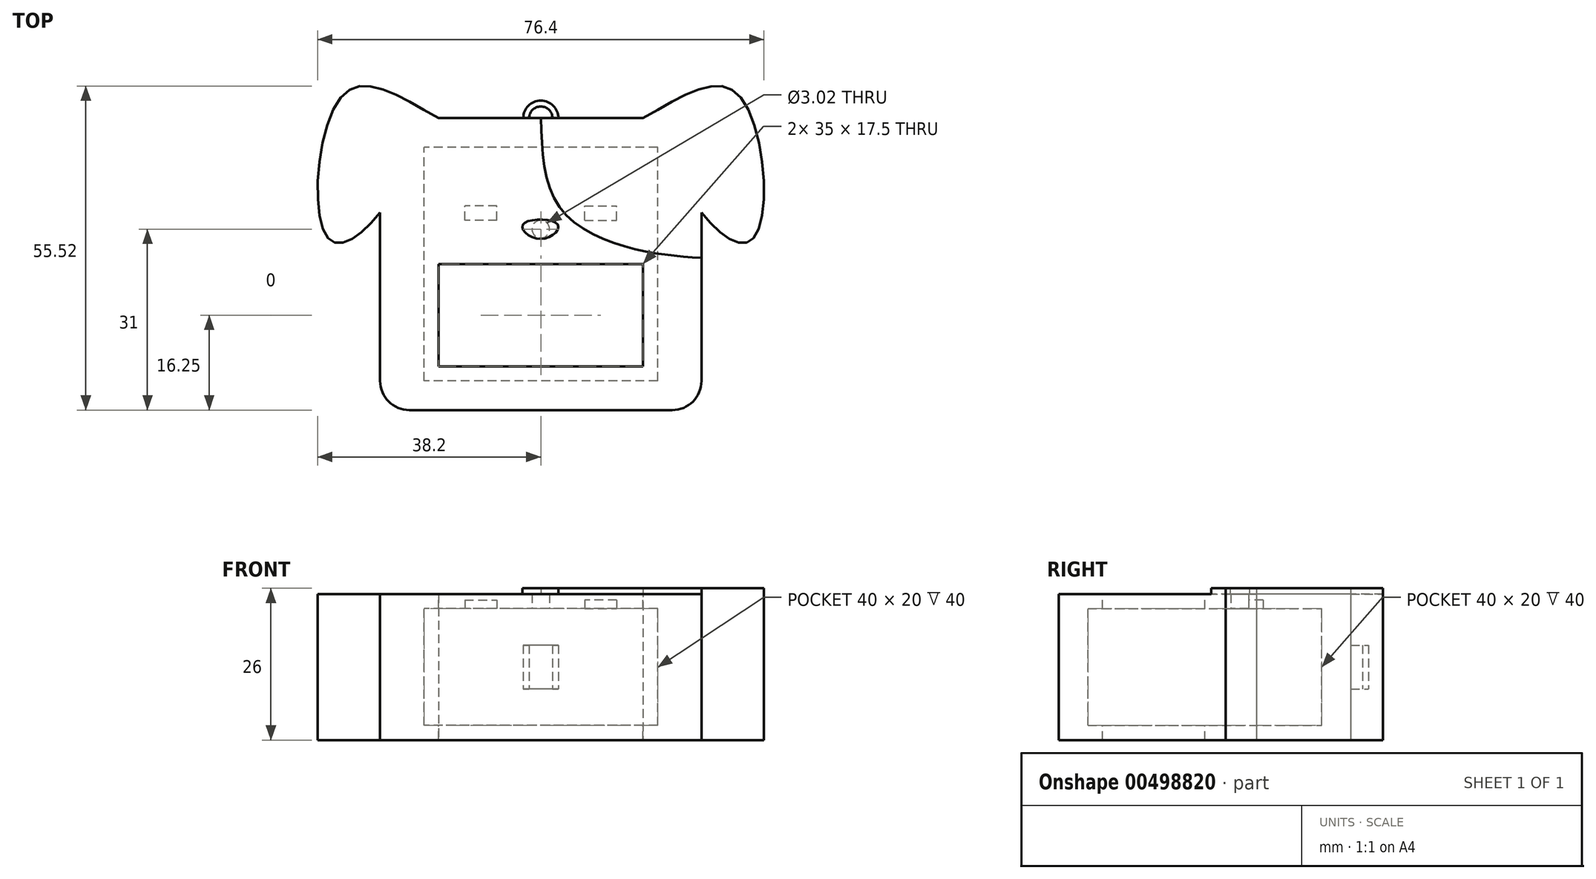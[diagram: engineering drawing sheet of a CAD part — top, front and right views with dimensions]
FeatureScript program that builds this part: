
annotation { "Feature Type Name" : "Feature", "Feature Type Description" : "" }
export const myFeature = defineFeature(function(context is Context, id is Id, definition is map)
    precondition{}
    {
        {
            var Q0;
            Q0=qCreatedBy(makeId("Top.planeOp"),FACE);
            var sketch = newSketch(context, id + "F0", { "sketchPlane" : qUnion([Q0])});
            skLineSegment(sketch, "E0.bottom", {"start": v(20, -20) * mm, "end": v(-20, -20) * mm});
            skLineSegment(sketch, "E0.top", {"start": v(20, 20) * mm, "end": v(-20, 20) * mm});
            skLineSegment(sketch, "E0.left", {"start": v(20, -20) * mm, "end": v(20, 20) * mm});
            skLineSegment(sketch, "E0.right", {"start": v(-20, -20) * mm, "end": v(-20, 20) * mm});
            skPoint(sketch, "E0.middle", {"position": v(0, 0) * mm});
            skSolve(sketch);
        }
        {
            var Q0;
            Q0=qCreatedBy(makeId("Top.planeOp"),FACE);
            var sketch = newSketch(context, id + "F1", { "sketchPlane" : qUnion([Q0])});
            skLineSegment(sketch, "E1.bottom", {"start": v(17.5, -17.5) * mm, "end": v(-17.5, -17.5) * mm});
            skLineSegment(sketch, "E1.left", {"start": v(17.5, -17.5) * mm, "end": v(17.5, 0) * mm});
            skLineSegment(sketch, "E1.right", {"start": v(-17.5, -17.5) * mm, "end": v(-17.5, 0) * mm});
            skPoint(sketch, "E1.middle", {"position": v(0, 0) * mm});
            skLineSegment(sketch, "E2", {"start": v(-17.5, 0) * mm, "end": v(17.5, 0) * mm});
            skPoint(sketch, "E1.top.start.orphan", {"position": v(17.5, 17.5) * mm});
            skPoint(sketch, "E3.orphan", {"position": v(-17.5, 17.5) * mm});
            skSolve(sketch);
        }
        {
            var Q0;
            Q0=qCreatedBy(makeId("Top.planeOp"),FACE);
            var sketch = newSketch(context, id + "F2", { "sketchPlane" : qUnion([Q0])});
            skLineSegment(sketch, "E4.bottom", {"start": v(27.5, -25) * mm, "end": v(-27.5, -25) * mm});
            skLineSegment(sketch, "E4.top", {"start": v(17.5, 25) * mm, "end": v(-17.5, 25) * mm});
            skLineSegment(sketch, "E4.left", {"start": v(27.5, -25) * mm, "end": v(27.5, 8.86) * mm});
            skLineSegment(sketch, "E4.right", {"start": v(-27.5, -25) * mm, "end": v(-27.5, 8.86) * mm});
            skPoint(sketch, "E4.middle", {"position": v(0, 0) * mm});
            skFitSpline(sketch, "E5", {"points": [v(-17.5, 25) * mm, v(-33.83, 29) * mm, v(-36.36, 4.35) * mm, v(-27.5, 8.86) * mm], "startDerivative": vector(-58.33, 32.73) * mm, "endDerivative": vector(34.15, 44.27) * mm});
            skFitSpline(sketch, "E6.MirrorCS", {"points": [v(17.5, 25) * mm, v(33.83, 29) * mm, v(36.36, 4.35) * mm, v(27.5, 8.86) * mm], "startDerivative": vector(58.33, 32.73) * mm, "endDerivative": vector(-34.15, 44.27) * mm});
            skPoint(sketch, "E7.orphan", {"position": v(-27.5, 25) * mm});
            skPoint(sketch, "E8.orphan", {"position": v(27.5, 25) * mm});
            skSolve(sketch);
        }
        {
            var Q0;
            Q0 = qSketchRegion(id + "F2", true);
            extrude(context, id + "F3", {"entities" : qUnion([Q0]), "endBound" : BoundingType.SYMMETRIC, "depth" : 25 * mm});
        }
        {
            var Q0;
            Q0 = qSketchRegion(id + "F0", true);
            extrude(context, id + "F4", {"entities" : qUnion([Q0]), "operationType" : NewBodyOperationType.REMOVE, "endBound" : BoundingType.SYMMETRIC, "oppositeDirection" : true, "depth" : 20 * mm});
        }
        {
            var Q0;
            Q0 = qSketchRegion(id + "F1", true);
            extrude(context, id + "F5", {"entities" : qUnion([Q0]), "operationType" : NewBodyOperationType.REMOVE, "endBound" : BoundingType.SYMMETRIC, "oppositeDirection" : true, "depth" : 25 * mm});
        }
        {
            var Q0;
            Q0=makeQuery(id+"F3.opExtrude","CAP_FACE",FACE,{"disambiguationData":[OSD([sQuery(id+"F2.wireOp",EDGE,"E4.bottom"),sQuery(id+"F2.wireOp",EDGE,"E4.top"),sQuery(id+"F2.wireOp",EDGE,"E4.left"),sQuery(id+"F2.wireOp",EDGE,"E4.right"),sQuery(id+"F2.wireOp",EDGE,"E5"),sQuery(id+"F2.wireOp",EDGE,"E6.MirrorCS")])],"isStart":false});
            var sketch = newSketch(context, id + "F6", { "sketchPlane" : qUnion([Q0])});
            skFitSpline(sketch, "E9", {"points": [v(0, 4.3) * mm, v(2.88, 6.8) * mm, v(-3.05, 6.8) * mm, v(0, 4.3) * mm]});
            skLineSegment(sketch, "E10", {"start": v(0, 4.3) * mm, "end": v(0, 0) * mm});
            skFitSpline(sketch, "E11", {"points": [v(0, 25) * mm, v(3.38, 9.53) * mm, v(16.34, 2.54) * mm, v(27.5, 1.07) * mm], "startDerivative": vector(1.76, -48.6) * mm, "endDerivative": vector(35.28, -2.44) * mm});
            skSolve(sketch);
        }
        {
            var Q0;
            Q0 = qSketchRegion(id + "F6", true);
            var Q1;
            Q1=sQuery(id+"F6.wireOp",EDGE,"E9");
            extrude(context, id + "F7", {"entities" : qUnion([Q0]), "surfaceEntities" : qUnion([Q1]), "depth" : 1 * mm});
        }
        {
            var Q0;
            Q0=qCreatedBy(makeId("Top.planeOp"),FACE);
            var sketch = newSketch(context, id + "F8", { "sketchPlane" : qUnion([Q0])});
            skArc(sketch, "E12", {"start": v(0, 28) * mm, "mid": v(2.12, 27.12) * mm, "end": v(3, 25) * mm});
            skArc(sketch, "E13.MirrorCS", {"start": v(0, 28) * mm, "mid": v(-2.12, 27.12) * mm, "end": v(-3, 25) * mm});
            skArc(sketch, "E14", {"start": v(0, 27) * mm, "mid": v(1.41, 26.41) * mm, "end": v(2, 25) * mm});
            skArc(sketch, "E15.MirrorCS", {"start": v(0, 27) * mm, "mid": v(-1.41, 26.41) * mm, "end": v(-2, 25) * mm});
            skLineSegment(sketch, "E16", {"start": v(-3, 25) * mm, "end": v(-2, 25) * mm});
            skLineSegment(sketch, "E17", {"start": v(2, 25) * mm, "end": v(3, 25) * mm});
            skSolve(sketch);
        }
        {
            var Q0;
            Q0 = qSketchRegion(id + "F8", true);
            extrude(context, id + "F9", {"entities" : qUnion([Q0]), "operationType" : NewBodyOperationType.ADD, "endBound" : BoundingType.SYMMETRIC, "depth" : 7.5 * mm});
        }
        {
            var Q0;
            {var subQ0=sQuery(id+"F6.wireOp",EDGE,"E11");Q0=makeQuery(id+"F6.imprint","IMPRINT",FACE,{"disambiguationData":[TD([[makeQuery(id+"F6.imprint","IMPRINT",EDGE,{"derivedFrom":subQ0}),1.0]])]});}
            extrude(context, id + "F10", {"entities" : qUnion([Q0]), "operationType" : NewBodyOperationType.ADD, "depth" : 1 * mm});
        }
        {
            var Q0;
            Q0=makeQuery(id+"F3.opExtrude","SWEPT_EDGE",EDGE,{"disambiguationData":[OSD([sQuery(id+"F2.wireOp",EDGE,"E4.bottom"),sQuery(id+"F2.wireOp",EDGE,"E4.left")])]});
            var Q1;
            Q1=makeQuery(id+"F3.opExtrude","SWEPT_EDGE",EDGE,{"disambiguationData":[OSD([sQuery(id+"F2.wireOp",EDGE,"E4.bottom"),sQuery(id+"F2.wireOp",EDGE,"E4.right")])]});
            fillet(context, id + "F11", {"entities" : qUnion([Q0, Q1]), "radius" : 5 * mm, "tangentPropagation" : true, "allowEdgeOverflow" : false});
        }
        {
            var Q0;
            Q0=qCreatedBy(makeId("Top.planeOp"),FACE);
            var sketch = newSketch(context, id + "F12", { "sketchPlane" : qUnion([Q0])});
            skLineSegment(sketch, "E18.bottom", {"start": v(-13, 10) * mm, "end": v(-7.5, 10) * mm});
            skLineSegment(sketch, "E18.top", {"start": v(-13, 7.5) * mm, "end": v(-7.5, 7.5) * mm});
            skLineSegment(sketch, "E18.left", {"start": v(-13, 10) * mm, "end": v(-13, 7.5) * mm});
            skLineSegment(sketch, "E18.right", {"start": v(-7.5, 10) * mm, "end": v(-7.5, 7.5) * mm});
            skCircle(sketch, "E19", {"center": v(0, 6) * mm, "radius": 1.51 * mm});
            skLineSegment(sketch, "E20.MirrorCS", {"start": v(13, 10) * mm, "end": v(7.5, 10) * mm});
            skLineSegment(sketch, "E21.MirrorCS", {"start": v(13, 10) * mm, "end": v(13, 7.5) * mm});
            skLineSegment(sketch, "E22.MirrorCS", {"start": v(13, 7.5) * mm, "end": v(7.5, 7.5) * mm});
            skLineSegment(sketch, "E23.MirrorCS", {"start": v(7.5, 10) * mm, "end": v(7.5, 7.5) * mm});
            skSolve(sketch);
        }
        {
            var Q0;
            Q0 = qSketchRegion(id + "F12", true);
            extrude(context, id + "F13", {"entities" : qUnion([Q0]), "operationType" : NewBodyOperationType.REMOVE, "depth" : 11.5 * mm});
        }
        {
            var Q0;
            Q0=qCreatedBy(makeId("Top.planeOp"),FACE);
            var sketch = newSketch(context, id + "F14", { "sketchPlane" : qUnion([Q0])});
            skCircle(sketch, "E24.0", {"center": v(0, 6) * mm, "radius": 1.51 * mm});
            skSolve(sketch);
        }
        {
            var Q0;
            Q0 = qSketchRegion(id + "F14", true);
            var Q1;
            Q1=sQuery(id+"F14.wireOp",EDGE,"b78d526f-3596-4bed-9b47-887e680bf16f.0");
            extrude(context, id + "F15", {"entities" : qUnion([Q0]), "operationType" : NewBodyOperationType.REMOVE, "surfaceEntities" : qUnion([Q1]), "depth" : 12.5 * mm});
        }
    });
